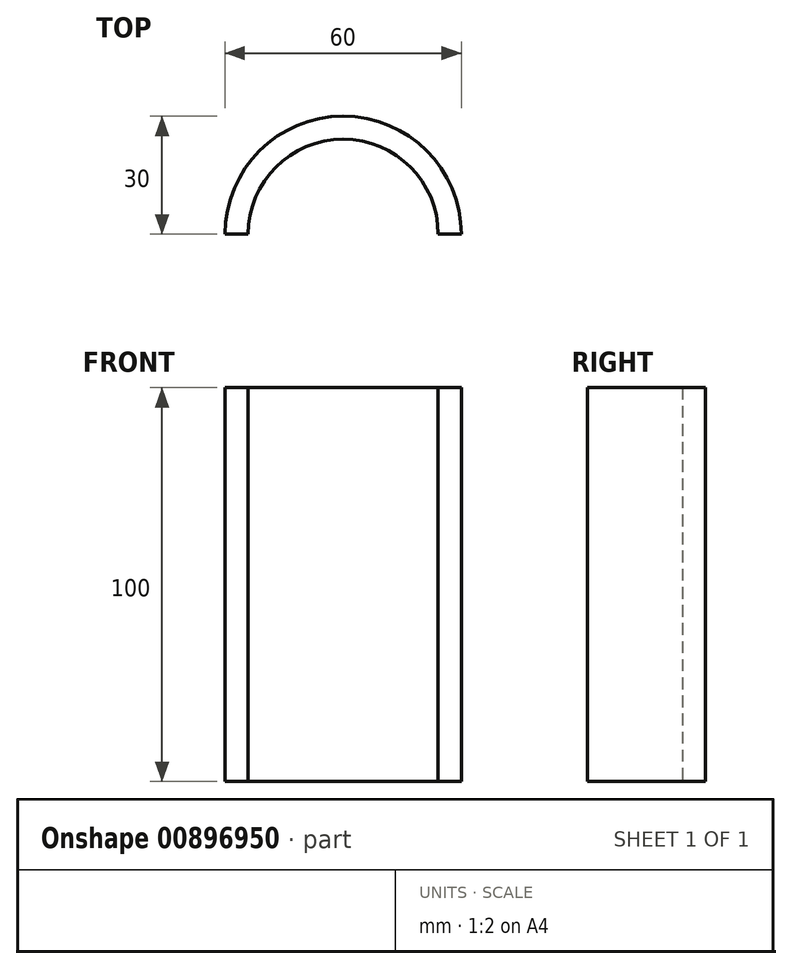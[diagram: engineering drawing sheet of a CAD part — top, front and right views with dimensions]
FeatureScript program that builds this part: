
annotation { "Feature Type Name" : "Feature", "Feature Type Description" : "" }
export const myFeature = defineFeature(function(context is Context, id is Id, definition is map)
    precondition{}
    {
        {
            var Q0;
            Q0=qCreatedBy(makeId("Top.planeOp"),FACE);
            var sketch = newSketch(context, id + "F0", { "sketchPlane" : qUnion([Q0])});
            skArc(sketch, "E0", {"start": v(24.15, 0) * mm, "mid": v(0, 24.15) * mm, "end": v(-24.15, 0) * mm});
            skArc(sketch, "E1", {"start": v(30, 0) * mm, "mid": v(0, 30) * mm, "end": v(-30, 0) * mm});
            skLineSegment(sketch, "E2", {"start": v(-30, 0) * mm, "end": v(-24.15, 0) * mm});
            skLineSegment(sketch, "E3.trimOffspring", {"start": v(24.15, 0) * mm, "end": v(30, 0) * mm});
            skSolve(sketch);
        }
        {
            var Q0;
            Q0 = qSketchRegion(id + "F0", true);
            extrude(context, id + "F1", {"entities" : qUnion([Q0]), "endBound" : BoundingType.SYMMETRIC, "depth" : 100 * mm, "offsetDistance" : 25 * mm});
        }
    });
